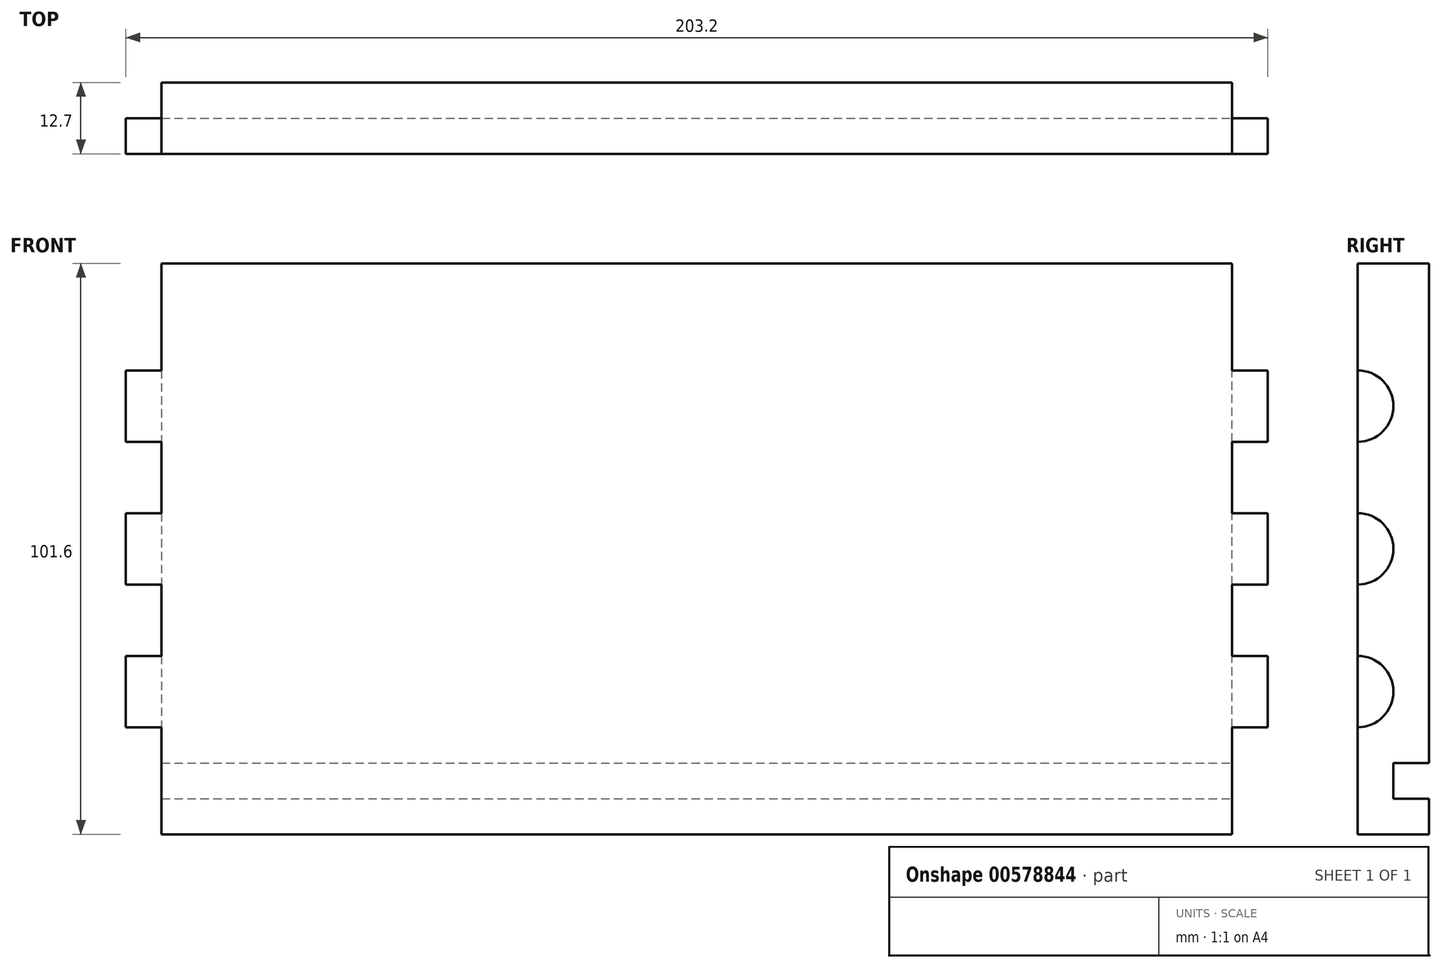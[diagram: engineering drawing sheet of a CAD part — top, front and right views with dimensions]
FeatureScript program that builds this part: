
annotation { "Feature Type Name" : "Feature", "Feature Type Description" : "" }
export const myFeature = defineFeature(function(context is Context, id is Id, definition is map)
    precondition{}
    {
        {
            var Q0;
            Q0=qCreatedBy(makeId("Front.planeOp"),FACE);
            var sketch = newSketch(context, id + "F0", { "sketchPlane" : qUnion([Q0])});
            skLineSegment(sketch, "E0.bottom", {"start": v(103.88, 50.8) * mm, "end": v(-99.32, 50.8) * mm});
            skLineSegment(sketch, "E0.top", {"start": v(103.88, -50.8) * mm, "end": v(-99.32, -50.8) * mm});
            skLineSegment(sketch, "E0.left", {"start": v(103.88, 50.8) * mm, "end": v(103.88, -50.8) * mm});
            skLineSegment(sketch, "E0.right", {"start": v(-99.32, 50.8) * mm, "end": v(-99.32, -50.8) * mm});
            skPoint(sketch, "E0.middle", {"position": v(2.28, 0) * mm});
            skLineSegment(sketch, "E1.bottom", {"start": v(-92.97, -38.1) * mm, "end": v(97.53, -38.1) * mm});
            skLineSegment(sketch, "E1.top", {"start": v(-92.97, -44.45) * mm, "end": v(97.53, -44.45) * mm});
            skLineSegment(sketch, "E1.left", {"start": v(-92.97, -38.1) * mm, "end": v(-92.97, -44.45) * mm});
            skLineSegment(sketch, "E1.right", {"start": v(97.53, -38.1) * mm, "end": v(97.53, -44.45) * mm});
            skLineSegment(sketch, "E2", {"start": v(-92.97, 50.8) * mm, "end": v(-92.97, -50.8) * mm});
            skLineSegment(sketch, "E3", {"start": v(97.53, 50.8) * mm, "end": v(97.53, -50.8) * mm});
            skSolve(sketch);
        }
        {
            var Q0;
            Q0 = qSketchRegion(id + "F0", true);
            var Q1;
            {var subQ0=sQuery(id+"F0.wireOp",EDGE,"E1.bottom");Q1=makeQuery(id+"F0.imprint","IMPRINT",FACE,{"disambiguationData":[TD([[makeQuery(id+"F0.imprint","IMPRINT",EDGE,{"derivedFrom":subQ0}),-1.0]])]});}
            extrude(context, id + "F1", {"entities" : qUnion([Q0, Q1]), "depth" : 12.7 * mm, "offsetDistance" : 25.4 * mm});
        }
        {
            var Q0;
            {var subQ0=sQuery(id+"F0.wireOp",EDGE,"E1.bottom");Q0=makeQuery(id+"F0.imprint","IMPRINT",FACE,{"disambiguationData":[TD([[makeQuery(id+"F0.imprint","IMPRINT",EDGE,{"derivedFrom":subQ0}),-1.0]])]});}
            extrude(context, id + "F2", {"entities" : qUnion([Q0]), "operationType" : NewBodyOperationType.REMOVE, "depth" : 6.35 * mm, "offsetDistance" : 25.4 * mm});
        }
        {
            var Q0;
            Q0=makeQuery(id+"F1.opExtrude","SWEPT_FACE",FACE,{"disambiguationData":[OSD([sQuery(id+"F0.wireOp",EDGE,"E0.right")])]});
            var sketch = newSketch(context, id + "F3", { "sketchPlane" : qUnion([Q0])});
            skArc(sketch, "E4", {"start": v(12.7, 31.75) * mm, "mid": v(6.35, 25.4) * mm, "end": v(12.7, 19.05) * mm});
            skArc(sketch, "E5", {"start": v(12.7, 6.35) * mm, "mid": v(6.35, 0) * mm, "end": v(12.7, -6.35) * mm});
            skArc(sketch, "E6", {"start": v(12.7, -19.05) * mm, "mid": v(6.35, -25.4) * mm, "end": v(12.7, -31.75) * mm});
            skSolve(sketch);
        }
        {
            var Q0;
            {var subQ4=sQuery(id+"F3.wireOp",EDGE,"E4");Q0=makeQuery(id+"F3.imprint","IMPRINT",FACE,{"disambiguationData":[TD([[makeQuery(id+"F3.imprint","IMPRINT",EDGE,{"derivedFrom":subQ4}),-1.0]])]});}
            extrude(context, id + "F4", {"entities" : qUnion([Q0]), "operationType" : NewBodyOperationType.REMOVE, "oppositeDirection" : true, "depth" : 6.35 * mm, "offsetDistance" : 25.4 * mm});
        }
        {
            var Q0;
            Q0=makeQuery(id+"F1.opExtrude","SWEPT_FACE",FACE,{"disambiguationData":[OSD([sQuery(id+"F0.wireOp",EDGE,"E0.left")])]});
            var sketch = newSketch(context, id + "F5", { "sketchPlane" : qUnion([Q0])});
            skArc(sketch, "E7", {"start": v(-12.7, 19.05) * mm, "mid": v(-6.35, 25.4) * mm, "end": v(-12.7, 31.75) * mm});
            skArc(sketch, "E8", {"start": v(-12.7, -6.35) * mm, "mid": v(-6.35, 0) * mm, "end": v(-12.7, 6.35) * mm});
            skArc(sketch, "E9", {"start": v(-12.7, -31.75) * mm, "mid": v(-6.35, -25.4) * mm, "end": v(-12.7, -19.05) * mm});
            skSolve(sketch);
        }
        {
            var Q0;
            Q0 = qSketchRegion(id + "F5", true);
            var Q1;
            {var subQ4=sQuery(id+"F5.wireOp",EDGE,"E7");Q1=makeQuery(id+"F5.imprint","IMPRINT",FACE,{"disambiguationData":[TD([[makeQuery(id+"F5.imprint","IMPRINT",EDGE,{"derivedFrom":subQ4}),-1.0]])]});}
            extrude(context, id + "F6", {"entities" : qUnion([Q0, Q1]), "operationType" : NewBodyOperationType.REMOVE, "oppositeDirection" : true, "depth" : 6.35 * mm, "offsetDistance" : 25.4 * mm});
        }
    });
